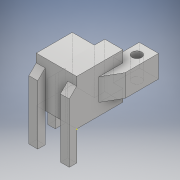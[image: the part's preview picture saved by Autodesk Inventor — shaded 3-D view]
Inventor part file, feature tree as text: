
AUTODESK INVENTOR PART (.ipt)
format: ipt  version: 2018 (Build 220112000, 112)  size: 180,736 bytes
history: native  units: mm
features: sketch x8, extrude x6, draft x3
ambient origin geometry x8: Origin, YZ Plane, XZ Plane, XY Plane, X Axis, Y Axis, Z Axis, Center Point
bodies: Solid1 (feature_tree)
feature tree (17):
  extrude  "Extrusion1"  Depth=30.7mm
  extrude  "Extrusion2"  Depth=7.7mm
  draft  "FaceDraft1"
  extrude  "Extrusion3"  Depth=15.0mm
  extrude  "Extrusion4"  TaperAngle=60.0deg  [1 undecoded]
  draft  "FaceDraft2"
  extrude  "Extrusion5"  Depth=6.45mm
  sketch  "Sketch6"  dims[d14=2.5mm d15=20.0mm d16=0.0mm]
  sketch  "Sketch7"  dims[d17=11.5mm]
  extrude  "Extrusion6"  Depth=20.0mm TaperAngle=0.0deg
  draft  "FaceDraft3"
  sketch  "Sketch1"  dims[d0=27.3mm d1=30.7mm]
  sketch  "Sketch2"  dims[d2=31.3mm d3=0.0mm d4=7.7mm]
  sketch  "Sketch3"  dims[d5=13.0mm d6=15.0mm]
  sketch  "Sketch4"  dims[d7=20.0mm d8=5.0mm d9=0.0mm d10=0.0mm d11=60.0deg]
  sketch  "Sketch5"  dims[d12=6.2mm d13=6.45mm]
  sketch  "Sketch8"  dims[d18=5.0mm d19=7.0mm d20=20.0mm d21=12.0mm d22=0.0mm d23=0.0mm d24=45.0deg d25=15.0mm d26=7.0mm d27=20.0mm d28=0.0mm d29=6.0mm d30=5.0mm d31=6.0mm d32=5.0mm d33=20.0mm d34=25.0mm d35=0.0mm d36=0.0mm d37=45.0deg]
note: 1 required parameter value undecoded (feature->parameter linkage not recoverable at this tier; creation-order binding heuristic only, values carry confidence <= 0.55)
